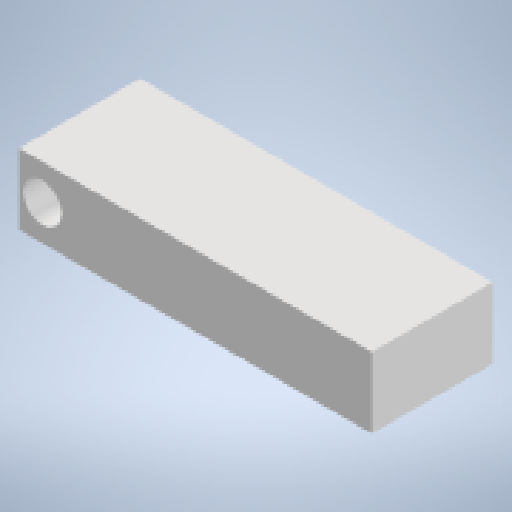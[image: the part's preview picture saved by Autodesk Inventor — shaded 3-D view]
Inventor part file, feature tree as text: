
AUTODESK INVENTOR PART (.ipt)
format: ipt  version: 2024.3 (Build 283343000, 343)  size: 139,264 bytes
history: native  units: mm
features: extrude x2, sketch x2, other x2, reference x1, projected_geometry x1
ambient origin geometry x8: Origin, YZ Plane, XZ Plane, XY Plane, X Axis, Y Axis, Z Axis, Center Point
bodies: Solid1 (feature_tree)
feature tree (8):
  extrude  "Extrusion1"  Depth=7.0mm
  extrude  "Extrusion2"  Depth=12.0mm
  sketch  "Sketch1"  dims[d0=35.0mm d1=7.0mm]
  reference  "Reference1"
  sketch  "Sketch2"  dims[d3=12.0mm d4=0.0mm d5=3.2mm d6=13.4mm d7=1.6mm d8=2.3mm d9=12.0mm d10=0.0mm]
  projected_geometry  "Projected Loop1"
  other  "Assembly1"
  other  "housing:1"
